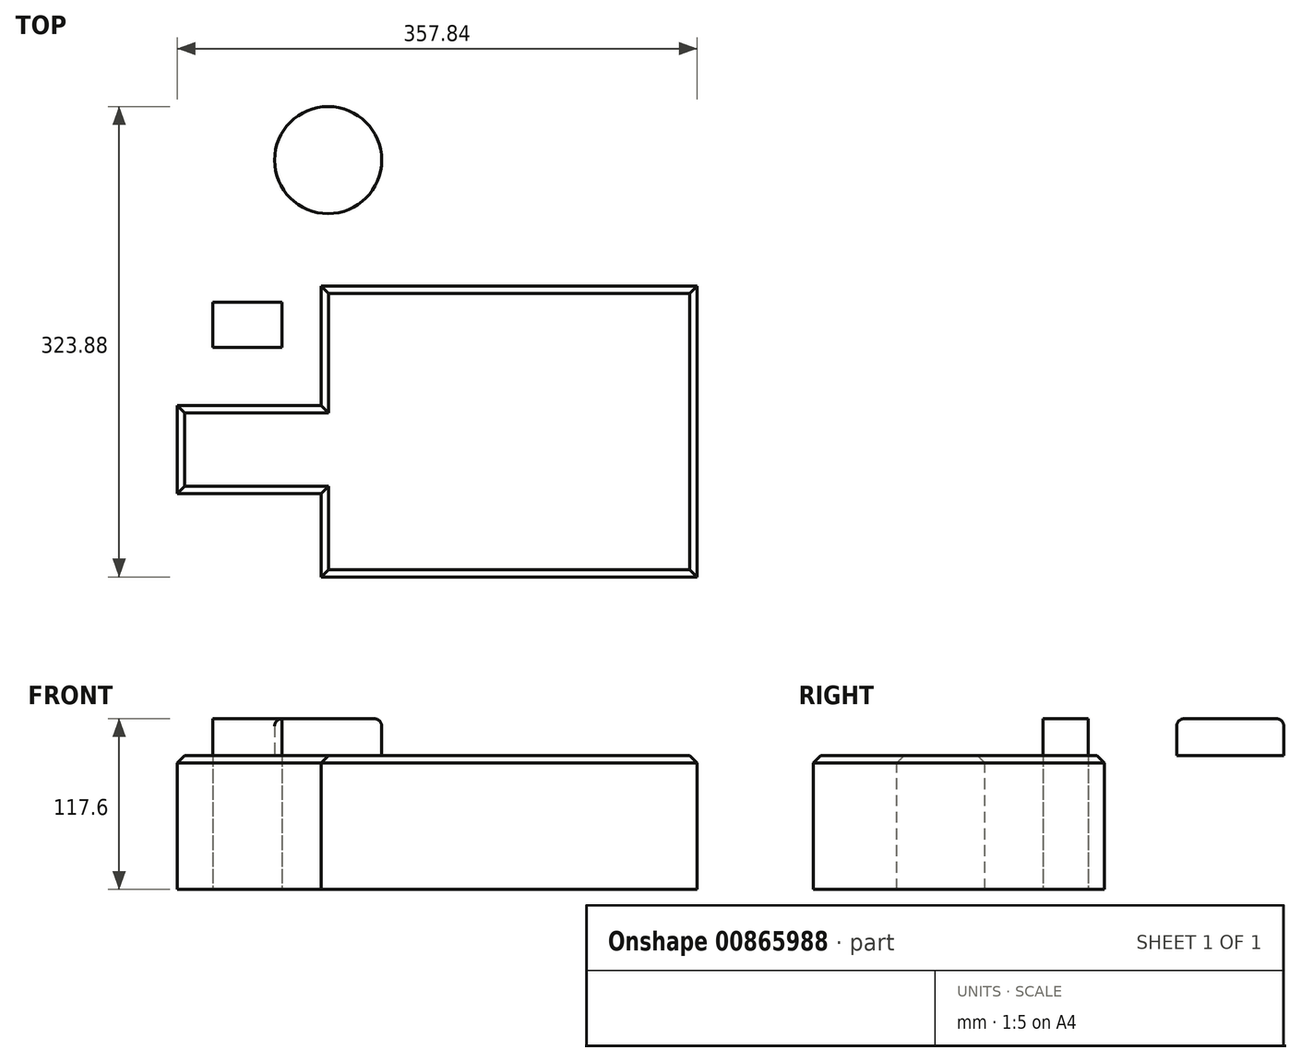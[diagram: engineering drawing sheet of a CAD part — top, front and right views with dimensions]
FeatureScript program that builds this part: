
annotation { "Feature Type Name" : "Feature", "Feature Type Description" : "" }
export const myFeature = defineFeature(function(context is Context, id is Id, definition is map)
    precondition{}
    {
        {
            var Q0;
            Q0=qCreatedBy(makeId("Top.planeOp"),FACE);
            var sketch = newSketch(context, id + "F0", { "sketchPlane" : qUnion([Q0])});
            skLineSegment(sketch, "E0.bottom", {"start": v(-114.46, 50.81) * mm, "end": v(144.3, 50.81) * mm});
            skLineSegment(sketch, "E0.top", {"start": v(-114.46, -149.52) * mm, "end": v(144.3, -149.52) * mm});
            skLineSegment(sketch, "E0.left", {"start": v(-114.46, 50.81) * mm, "end": v(-114.46, -149.52) * mm});
            skLineSegment(sketch, "E0.right", {"start": v(144.3, 50.81) * mm, "end": v(144.3, -149.52) * mm});
            skLineSegment(sketch, "E1.bottom", {"start": v(-114.46, -31.45) * mm, "end": v(-213.55, -31.45) * mm});
            skLineSegment(sketch, "E1.top", {"start": v(-114.46, -92.18) * mm, "end": v(-213.55, -92.18) * mm});
            skLineSegment(sketch, "E1.left", {"start": v(-114.46, -31.45) * mm, "end": v(-114.46, -92.18) * mm});
            skLineSegment(sketch, "E1.right", {"start": v(-213.55, -31.45) * mm, "end": v(-213.55, -92.18) * mm});
            skLineSegment(sketch, "E2.bottom", {"start": v(-189.01, 39.65) * mm, "end": v(-141.32, 39.65) * mm});
            skLineSegment(sketch, "E2.top", {"start": v(-189.01, 8.47) * mm, "end": v(-141.32, 8.47) * mm});
            skLineSegment(sketch, "E2.left", {"start": v(-189.01, 39.65) * mm, "end": v(-189.01, 8.47) * mm});
            skLineSegment(sketch, "E2.right", {"start": v(-141.32, 39.65) * mm, "end": v(-141.32, 8.47) * mm});
            skSolve(sketch);
        }
        {
            var Q0;
            Q0=makeQuery(id+"F0.imprint","IMPRINT",FACE,{"disambiguationData":[TD([[makeQuery(id+"F0.imprint","IMPRINT",EDGE,{"derivedFrom":sQuery(id+"F0.wireOp",EDGE,"E2.bottom")}),-1.0]])]});
            extrude(context, id + "F1", {"entities" : qUnion([Q0]), "depth" : 25.4 * mm, "offsetDistance" : 25.4 * mm});
        }
        {
            var Q0;
            Q0 = qSketchRegion(id + "F0", true);
            extrude(context, id + "F2", {"entities" : qUnion([Q0]), "operationType" : NewBodyOperationType.ADD, "oppositeDirection" : true, "depth" : 92.2 * mm, "offsetDistance" : 25.4 * mm});
        }
        {
            var Q0;
            Q0=qCreatedBy(makeId("Top.planeOp"),FACE);
            var sketch = newSketch(context, id + "F3", { "sketchPlane" : qUnion([Q0])});
            skCircle(sketch, "E3", {"center": v(-109.68, 137.5) * mm, "radius": 36.86 * mm});
            skSolve(sketch);
        }
        {
            var Q0;
            Q0=makeQuery(id+"F3.imprint","IMPRINT",FACE,{"disambiguationData":[TD([[makeQuery(id+"F3.imprint","IMPRINT",EDGE,{"derivedFrom":sQuery(id+"F3.wireOp",EDGE,"E3")}),1.0]])]});
            extrude(context, id + "F4", {"entities" : qUnion([Q0]), "depth" : 25.4 * mm, "offsetDistance" : 25.4 * mm});
        }
        {
            var Q0;
            Q0=makeQuery(id+"F4.opExtrude","CAP_EDGE",EDGE,{"disambiguationData":[OSD([sQuery(id+"F3.wireOp",EDGE,"E3")])],"isStart":false});
            fillet(context, id + "F5", {"entities" : qUnion([Q0]), "radius" : 5.08 * mm, "tangentPropagation" : true, "allowEdgeOverflow" : false});
        }
        {
            var Q0;
            Q0=makeQuery(id+"F2.opExtrude","CAP_FACE",FACE,{"disambiguationData":[OSD([sQuery(id+"F0.wireOp",EDGE,"E0.bottom"),sQuery(id+"F0.wireOp",EDGE,"E0.top"),sQuery(id+"F0.wireOp",EDGE,"E0.left"),sQuery(id+"F0.wireOp",EDGE,"E0.right"),sQuery(id+"F0.wireOp",EDGE,"E1.bottom"),sQuery(id+"F0.wireOp",EDGE,"E1.top"),sQuery(id+"F0.wireOp",EDGE,"E1.right")])],"isStart":true});
            chamfer(context, id + "F6", {"entities" : qUnion([Q0]), "width" : 5.08 * mm, "tangentPropagation" : true});
        }
    });
